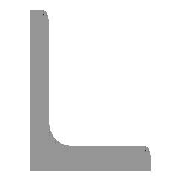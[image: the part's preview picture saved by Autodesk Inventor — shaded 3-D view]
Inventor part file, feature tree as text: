
AUTODESK INVENTOR PART (.ipt)
format: ipt  version: 2024.1 (Build 281209000, 209)  size: 120,832 bytes
history: native  units: mm (DEFAULTED — no unit token found)
features: other x4, sketch x1, plane x1
ambient origin geometry x8: Origin, YZ Plane, XZ Plane, XY Plane, X Axis, Y Axis, Z Axis, Center Point
bodies: Solid1 (feature_tree), Body (feature_tree)
feature tree (6):
  parser-record x1  (decoder bookkeeping rows leaked as tree rows — omitted from the tree; the rows remain in map.json)
  other  "Driven Length"
  other  "Start Plane"
  other  "End Plane"
  sketch  "Sketch3"  dims[d0=28.702mm d1=28.702mm d2=3.175mm d3=3.175mm d4=960.0mm d5=0.0mm d10=0.0mm d11=0.0mm d12=-0.0mm d13=960.0mm d14=2.286mm d15=1.27mm d16=90.0deg d17=960.0mm]
  plane  "Work Plane3"
